# Revit family: Betty TK1
name_source: partatom
category: Furniture
revit_build: Autodesk Revit 2017 (Build: 20171027_0315(x64)
units: mm (PartAtom-declared; Revit-internal decimal feet)

## family parameters
Always vertical = Yes
Cut with Voids When Loaded = No
OmniClass Number = 23.40.20.00
OmniClass Title = General Furniture and Specialties
Room Calculation Point = No
Shared = No
Work Plane-Based = No

## types (1)
- Betty TK1
    Backrest = &tradition Lacquered Oak Horizontal
    Base = &tradition Lacquered Oak Vertical
    Depth = 48cm/18.9in
    Description = Designers Jakob Thau & Sami Kallio have created a chair that champions a design element usually concealed: the supportive seat webbing.
    Design = Thau & Kallio
    Design Year = 2019
    Frame = &tradition Lacquered Oak Horizontal
    Gliders = &tradition Felt Black
    Height = 77cm/30.3in
    Manufacturer = &tradition
    Model = Betty Chair TK1
    Packaging Dimensions = H: 72cm/28.4in, W: 67cm/26.8in, D: 70cm/27.6in
    Seat Height = 46cm/18.1in
    Seat Webbing 01 = &tradition Natural linen webbing Horizontal
    Seat Webbing 02 = &tradition Natural linen webbing Vertical
    Stacking = Stackable
    Type Comments = Betty Series
    URL = https://www.andtradition.com
    Variations frame colour = Available in oiled oak, lacquered ash Twilight  and lacquered ash Maroon
    Weight = 4kg
    Width = 51cm/20.1in

## geometry (parser evidence)
native form markers: Sweep x2
no freeform markers — native parametric forms only
